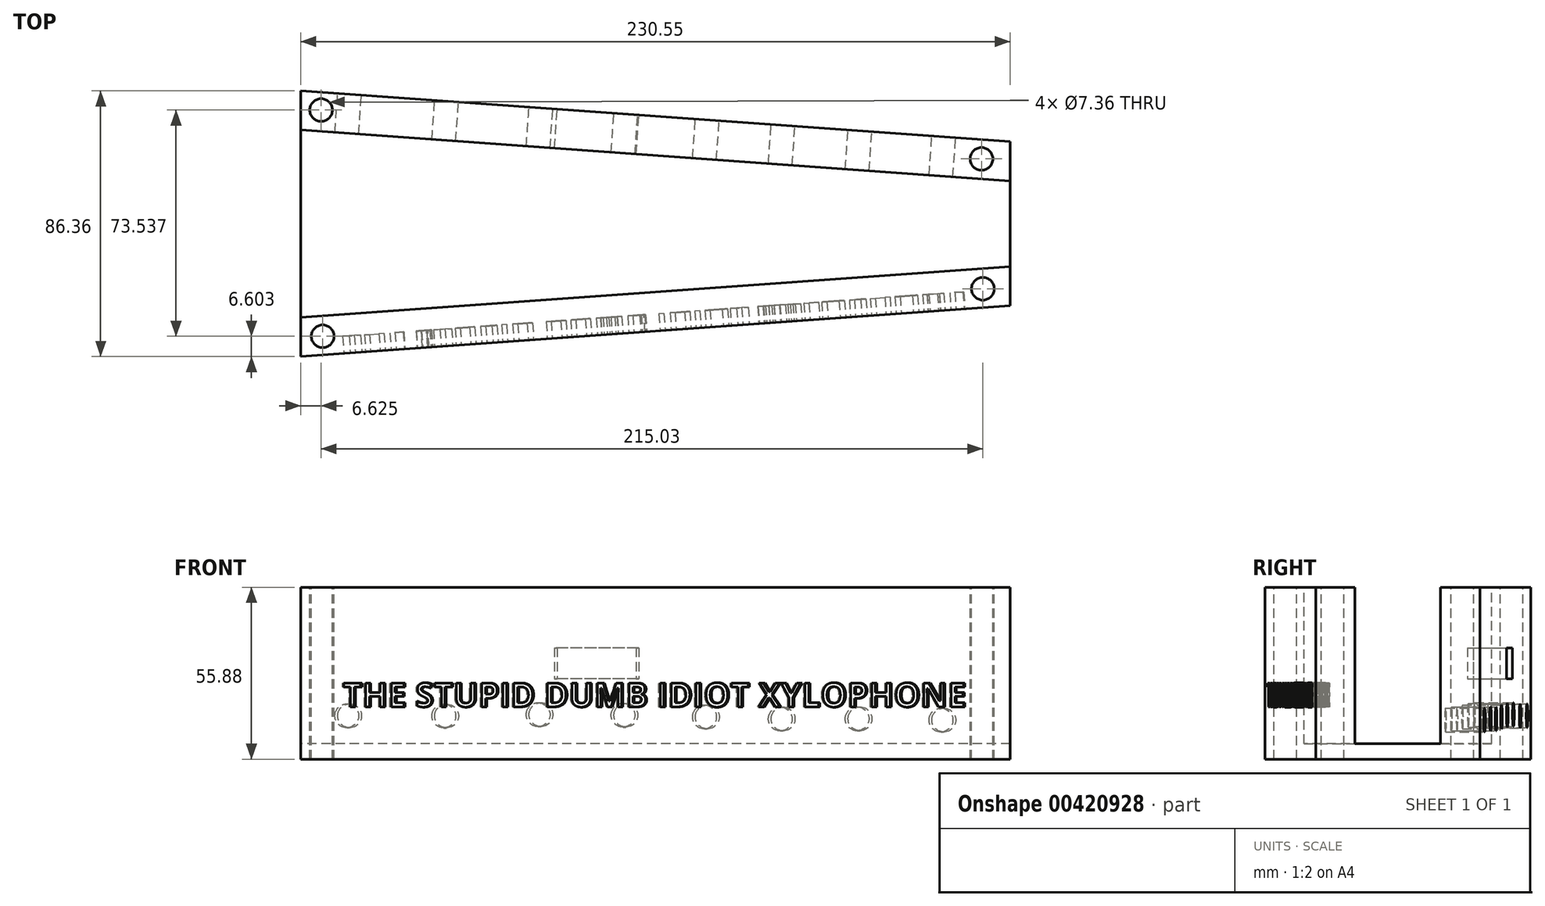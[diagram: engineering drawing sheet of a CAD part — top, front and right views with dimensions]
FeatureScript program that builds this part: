
annotation { "Feature Type Name" : "Feature", "Feature Type Description" : "" }
export const myFeature = defineFeature(function(context is Context, id is Id, definition is map)
    precondition{}
    {
        {
            var Q0;
            Q0=qCreatedBy(makeId("Top.planeOp"),FACE);
            var sketch = newSketch(context, id + "F0", { "sketchPlane" : qUnion([Q0])});
            skLineSegment(sketch, "E0", {"start": v(28.33, 44.1) * mm, "end": v(28.33, -42.26) * mm});
            skLineSegment(sketch, "E1", {"start": v(28.33, -42.26) * mm, "end": v(258.88, -25.75) * mm});
            skLineSegment(sketch, "E2", {"start": v(258.88, -25.75) * mm, "end": v(258.88, 27.59) * mm});
            skLineSegment(sketch, "E3", {"start": v(258.88, 27.59) * mm, "end": v(28.33, 44.1) * mm});
            skSolve(sketch);
        }
        {
            var Q0;
            Q0 = qSketchRegion(id + "F0", true);
            extrude(context, id + "F1", {"entities" : qUnion([Q0]), "depth" : 55.88 * mm});
        }
        {
            var Q0;
            Q0=makeQuery(id+"F1.opExtrude","CAP_FACE",FACE,{"disambiguationData":[OSD([sQuery(id+"F0.wireOp",EDGE,"E0"),sQuery(id+"F0.wireOp",EDGE,"E1"),sQuery(id+"F0.wireOp",EDGE,"E2"),sQuery(id+"F0.wireOp",EDGE,"E3")])],"isStart":false});
            var sketch = newSketch(context, id + "F2", { "sketchPlane" : qUnion([Q0])});
            skLineSegment(sketch, "E4", {"start": v(28.33, 31.4) * mm, "end": v(28.33, -29.53) * mm});
            skLineSegment(sketch, "E5", {"start": v(28.33, -29.53) * mm, "end": v(258.88, -13.02) * mm});
            skLineSegment(sketch, "E6", {"start": v(258.88, -13.02) * mm, "end": v(258.88, 14.84) * mm});
            skLineSegment(sketch, "E7", {"start": v(258.88, 14.84) * mm, "end": v(28.33, 31.4) * mm});
            skSolve(sketch);
        }
        {
            var Q0;
            Q0 = qSketchRegion(id + "F2", true);
            extrude(context, id + "F3", {"entities" : qUnion([Q0]), "operationType" : NewBodyOperationType.REMOVE, "oppositeDirection" : true, "depth" : 50.8 * mm});
        }
        {
            var Q0;
            Q0=makeQuery(id+"F1.opExtrude","SWEPT_FACE",FACE,{"disambiguationData":[OSD([sQuery(id+"F0.wireOp",EDGE,"E3")])]});
            var sketch = newSketch(context, id + "F4", { "sketchPlane" : qUnion([Q0])});
            skCircle(sketch, "E8", {"center": v(-234.6, 12.73) * mm, "radius": 3.88 * mm});
            skCircle(sketch, "E9", {"center": v(-207.3, 13.15) * mm, "radius": 3.88 * mm});
            skCircle(sketch, "E10", {"center": v(-182.24, 13.1) * mm, "radius": 3.88 * mm});
            skCircle(sketch, "E11", {"center": v(-157.56, 13.75) * mm, "radius": 3.88 * mm});
            skCircle(sketch, "E12", {"center": v(-131.03, 14.32) * mm, "radius": 3.88 * mm});
            skCircle(sketch, "E13", {"center": v(-103.37, 14.5) * mm, "radius": 3.88 * mm});
            skCircle(sketch, "E14", {"center": v(-72.64, 14.06) * mm, "radius": 3.88 * mm});
            skCircle(sketch, "E15", {"center": v(-41.03, 14.12) * mm, "radius": 3.88 * mm});
            skSolve(sketch);
        }
        {
            var Q0;
            Q0 = qSketchRegion(id + "F4", true);
            extrude(context, id + "F5", {"entities" : qUnion([Q0]), "operationType" : NewBodyOperationType.REMOVE, "oppositeDirection" : true, "depth" : 14.22 * mm});
        }
        {
            var Q0;
            Q0=makeQuery(id+"F1.opExtrude","SWEPT_FACE",FACE,{"disambiguationData":[OSD([sQuery(id+"F0.wireOp",EDGE,"E3")])]});
            var sketch = newSketch(context, id + "F6", { "sketchPlane" : qUnion([Q0])});
            skLineSegment(sketch, "E16.bottom", {"start": v(-135.3, 36.2) * mm, "end": v(-108.68, 36.2) * mm});
            skLineSegment(sketch, "E16.top", {"start": v(-135.3, 26.13) * mm, "end": v(-108.68, 26.13) * mm});
            skLineSegment(sketch, "E16.left", {"start": v(-135.3, 36.2) * mm, "end": v(-135.3, 26.13) * mm});
            skLineSegment(sketch, "E16.right", {"start": v(-108.68, 36.2) * mm, "end": v(-108.68, 26.13) * mm});
            skSolve(sketch);
        }
        {
            var Q0;
            Q0 = qSketchRegion(id + "F6", true);
            extrude(context, id + "F7", {"entities" : qUnion([Q0]), "operationType" : NewBodyOperationType.REMOVE, "oppositeDirection" : true, "depth" : 15.24 * mm});
        }
        {
            var Q0;
            Q0=makeQuery(id+"F1.opExtrude","SWEPT_FACE",FACE,{"disambiguationData":[OSD([sQuery(id+"F0.wireOp",EDGE,"E1")])]});
            var sketch = newSketch(context, id + "F8", { "sketchPlane" : qUnion([Q0])});
            skText(sketch, "E17", { "text": "THE STUPID DUMB IDIOT XYLOPHONE", "fontName": "OpenSans-Bold.ttf"});
            const initialGuessF8  = {"E17": [0.0391, 0.01702, 1, 0, 0.00785]};
            skSetInitialGuess(sketch, initialGuessF8);
            skSolve(sketch);
        }
        {
            var Q0;
            {var subQ0=sQuery(id+"F0.wireOp",EDGE,"E0");var subQ1=sQuery(id+"F0.wireOp",EDGE,"E1");var subQ2=sQuery(id+"F0.wireOp",EDGE,"E2");Q0=makeQuery(id+"F3.boolean.opBoolean","SPLIT",FACE,{"disambiguationData":[TD([makeQuery(id+"F1.opExtrude","SWEPT_FACE",FACE,{"disambiguationData":[OSD([subQ1])]})])],"derivedFrom":makeQuery(id+"F1.opExtrude","CAP_FACE",FACE,{"disambiguationData":[OSD([subQ0,subQ1,subQ2,sQuery(id+"F0.wireOp",EDGE,"E3")])],"isStart":false})});}
            var sketch = newSketch(context, id + "F9", { "sketchPlane" : qUnion([Q0])});
            skCircle(sketch, "E18", {"center": v(35.47, -35.66) * mm, "radius": 3.68 * mm});
            skCircle(sketch, "E19", {"center": v(34.95, 37.88) * mm, "radius": 3.68 * mm});
            skCircle(sketch, "E20", {"center": v(249.54, 21.99) * mm, "radius": 3.68 * mm});
            skCircle(sketch, "E21", {"center": v(249.98, -20.22) * mm, "radius": 3.68 * mm});
            skSolve(sketch);
        }
        {
            var Q0;
            Q0 = qSketchRegion(id + "F9", true);
            extrude(context, id + "F10", {"entities" : qUnion([Q0]), "operationType" : NewBodyOperationType.REMOVE, "oppositeDirection" : true, "depth" : 61.47 * mm});
        }
        {
            var Q0;
            Q0 = qSketchRegion(id + "F8", true);
            extrude(context, id + "F11", {"entities" : qUnion([Q0]), "operationType" : NewBodyOperationType.REMOVE, "oppositeDirection" : true, "depth" : 5.6 * mm});
        }
    });
